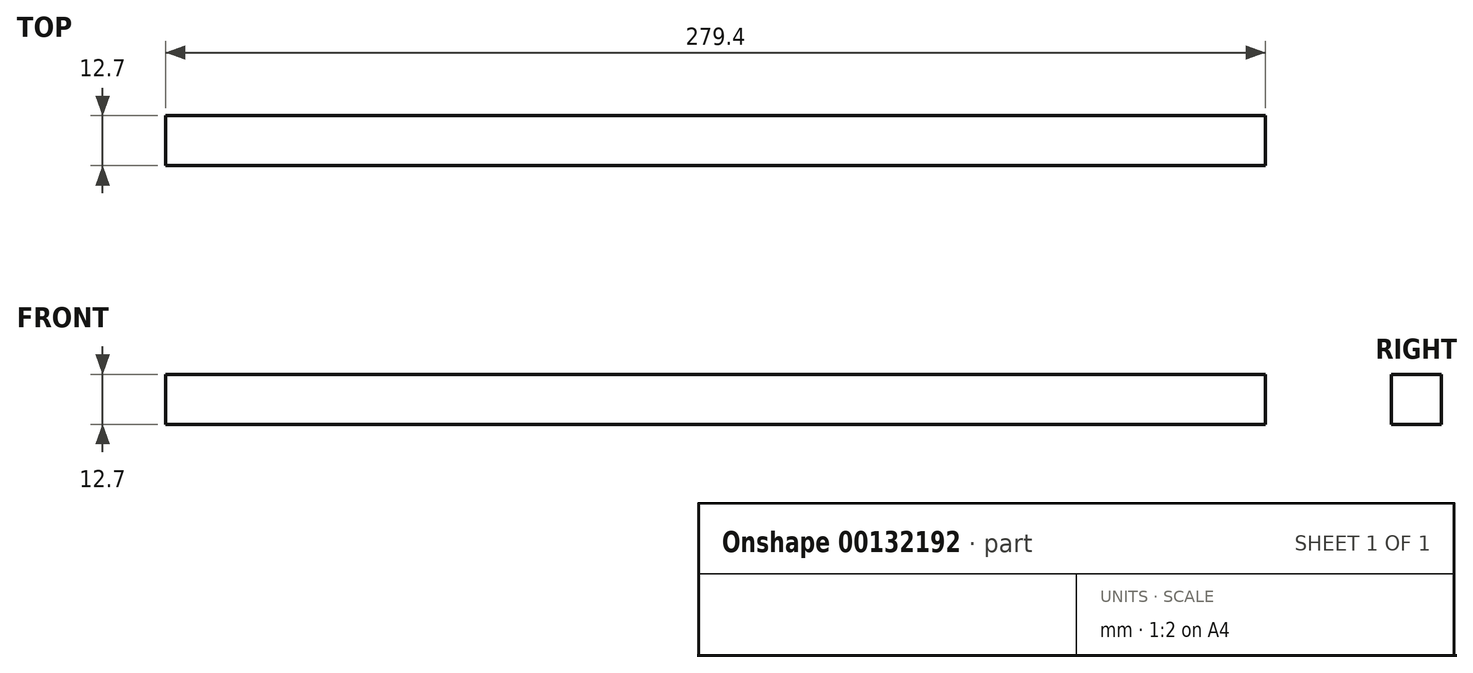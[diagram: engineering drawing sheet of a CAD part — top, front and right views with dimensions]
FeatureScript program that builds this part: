
annotation { "Feature Type Name" : "Feature", "Feature Type Description" : "" }
export const myFeature = defineFeature(function(context is Context, id is Id, definition is map)
    precondition{}
    {
        {
            var Q0;
            Q0=qCreatedBy(makeId("Front.planeOp"),FACE);
            var sketch = newSketch(context, id + "F0", { "sketchPlane" : qUnion([Q0])});
            skLineSegment(sketch, "E0.bottom", {"start": v(0, 0) * mm, "end": v(279.4, 0) * mm});
            skLineSegment(sketch, "E0.top", {"start": v(0, 12.7) * mm, "end": v(279.4, 12.7) * mm});
            skLineSegment(sketch, "E0.left", {"start": v(0, 0) * mm, "end": v(0, 12.7) * mm});
            skLineSegment(sketch, "E0.right", {"start": v(279.4, 0) * mm, "end": v(279.4, 12.7) * mm});
            skSolve(sketch);
        }
        {
            var Q0;
            Q0 = qSketchRegion(id + "F0", true);
            extrude(context, id + "F1", {"entities" : qUnion([Q0]), "depth" : 12.7 * mm});
        }
    });
